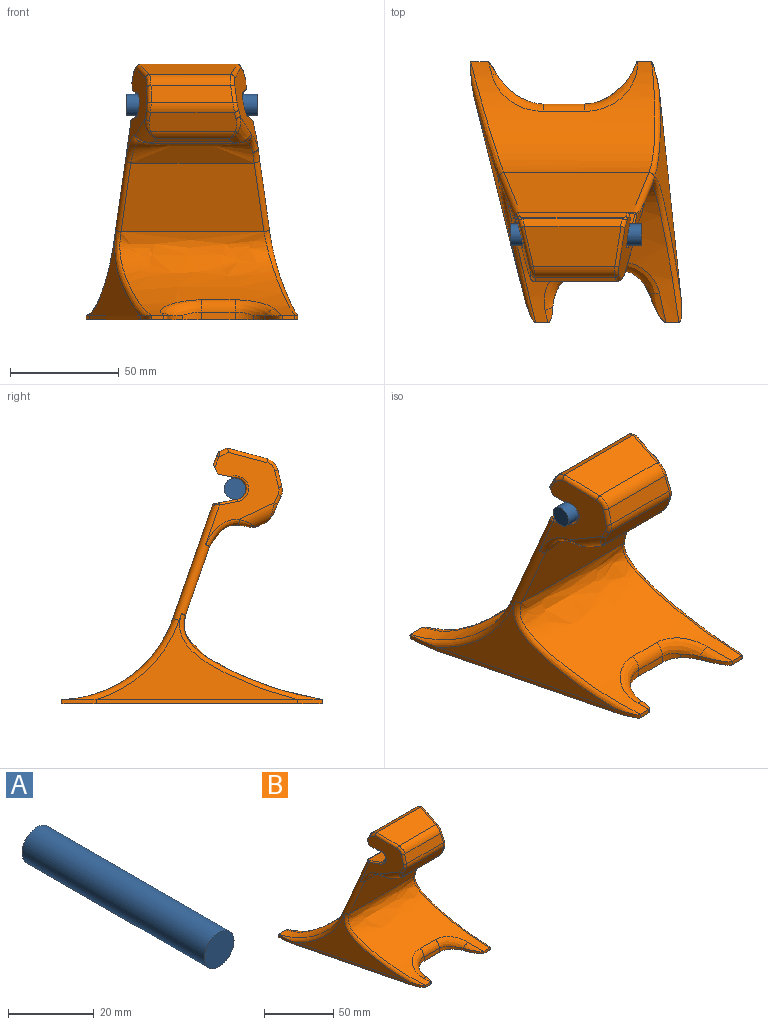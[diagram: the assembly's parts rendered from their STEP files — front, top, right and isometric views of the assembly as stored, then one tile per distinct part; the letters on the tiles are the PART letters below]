
ASSEMBLY  parts=2 mates=1
PART A: 3 faces, bbox 9.8x60x9.8 mm
  f0: cylinder r=4.9mm len=60mm, axis (0,1,0), area 1847.3mm2, adj f1,f2
  f1: plane 9.8x9.8mm, normal (0,-1,0), area 75.4mm2, adj f0
  f2: plane 9.8x9.8mm, normal (0,1,0), area 75.4mm2, adj f0
PART B: 107 faces, bbox 101.3x139.5x139.7 mm
  f0: bspline ~123.3x69.06mm, area 557mm2, adj f30,f62,f63,f69,f70,f71,f72,f77
  f1: plane 42.46x33.79mm, normal (-0.97,-0.24,0.05), area 579.7mm2, adj f13,f19,f31,f33,f65,f67,f73,f74
  f2: plane 95.15x39.86mm, normal (0.98,0.1,0.17), area 1113.8mm2, adj f26,f27,f28,f58
  f3: plane 92.77x39.56mm, normal (-0.97,-0.24,0.05), area 1096.3mm2, adj f32,f33,f34,f50
  f4: cylinder r=55.44mm len=83.31mm, axis (-1,0,0), area 3679.6mm2, adj f10,f26,f34,f40,f41,f42,f43,f52
  f5: plane 44.65x18.45mm, normal (0,-0.26,0.97), area 781.6mm2, adj f18,f69,f70,f75,f76,f78
  f6: plane 40.4x8.66mm, normal (0,-0.91,-0.41), area 376.6mm2, adj f72,f73,f81,f83,f88,f91
  f7: extruded ~56.76x17.9mm, area 1162.2mm2, adj f8,f29,f30,f31,f84,f89,f92
  f8: plane 65.74x31.62mm, normal (0,-0.94,-0.33), area 2052.5mm2, adj f7,f9,f27,f29,f31,f33
  f9: extruded ~80.56x63.79mm, area 4079.8mm2, adj f8,f27,f28,f32,f33,f35,f36,f37
  f10: plane 66.6x52.31mm, normal (0,0.94,0.33), area 3282.4mm2, adj f4,f27,f33,f66
  f11: plane 54.15x10.49mm, normal (0,0.18,0.98), area 555.2mm2, adj f12,f63,f64,f66,f67,f68
  f12: cylinder r=5mm len=49.57mm, axis (-1,0,0), area 661.6mm2, adj f11,f13,f62,f65
  f13: plane 51.77x9.13mm, normal (0,0.21,-0.98), area 445.6mm2, adj f1,f12,f19,f65,f95,f96
  f14: plane 50.31x5.37mm, normal (0,0.91,0.41), area 287.8mm2, adj f19,f96,f97,f98,f99,f100,f101
  f15: plane 10.19x3.56mm, normal (0.98,0.1,0.17), area 6.8mm2, adj f27,f29,f104
  f16: plane 37.7x7.8mm, normal (0,-0.97,0.23), area 298mm2, adj f71,f74,f78,f81
  f17: plane 35.23x3.01mm, normal (0,-0.43,-0.9), area 114.7mm2, adj f85,f88,f89,f94
  f18: plane 45.95x3.46mm, normal (0,0.43,0.9), area 172.7mm2, adj f5,f69,f76,f99
  f19: plane 51.94x4.81mm, normal (0,0.89,-0.45), area 258.7mm2, adj f1,f13,f14,f96,f101
  f20: plane 19.04x2.1mm, normal (0,1,0), area 40mm2, adj f22,f23,f41,f61
  f21: plane 15.54x3.61mm, normal (0,-1,0), area 56.1mm2, adj f24,f25,f38,f61
  f22: cylinder r=18.29mm len=2.41mm, axis (0,0,1), area 4.9mm2, adj f20,f40,f55,f61
  f23: cylinder r=18.29mm len=2.41mm, axis (0,0,1), area 4.9mm2, adj f20,f43,f54,f61
  f24: cylinder r=13.01mm len=8.48mm, axis (0,0,1), area 25.9mm2, adj f21,f36,f45,f61
  f25: cylinder r=13.01mm len=8.48mm, axis (0,0,1), area 25.9mm2, adj f21,f39,f46,f61
  f26: bspline ~53.44x39.28mm, area 212.6mm2, adj f2,f4,f27,f57
  f27: cylinder r=2.5mm len=54.06mm, axis (0.13,0.33,-0.94), area 334.9mm2, adj f2,f8,f9,f10,f15,f26,f28,f29
  f28: bspline ~68.14x42.43mm, area 295.3mm2, adj f2,f9,f27,f59
  f29: bspline ~8.97x7.02mm, area 26.7mm2, adj f7,f8,f15,f27,f102,f103
  f30: bspline ~12.73x8.67mm, area 48.5mm2, adj f0,f7,f92,f102
  f31: bspline ~17.65x13.1mm, area 71.1mm2, adj f1,f7,f8,f33,f84
  f32: bspline ~67.71x42.29mm, area 277.8mm2, adj f3,f9,f33,f49
  f33: cylinder r=2.5mm len=54.81mm, axis (-0.13,0.33,-0.94), area 365.3mm2, adj f1,f3,f8,f9,f10,f31,f32,f34
  f34: bspline ~54.1x39.59mm, area 261.5mm2, adj f3,f4,f33,f51
  f35: bspline ~19.35x9.82mm, area 40.6mm2, adj f9,f36,f44
  f36: bspline ~21.47x16.35mm, area 157mm2, adj f9,f24,f35,f38,f45
  f37: bspline ~16.44x9.13mm, area 11.6mm2, adj f9,f39,f47
  f38: cylinder r=6mm len=15.54mm, axis (-1,0,0), area 113.4mm2, adj f9,f21,f36,f39
  f39: bspline ~23.47x21.67mm, area 192.3mm2, adj f9,f25,f37,f38,f46
  f40: bspline ~26.88x24.14mm, area 140.9mm2, adj f4,f22,f41,f55
  f41: cylinder r=6mm len=19.04mm, axis (-1,0,0), area 128mm2, adj f4,f20,f40,f43
  f42: bspline ~21.17x10.9mm, area 6.9mm2, adj f4,f43,f53
  f43: bspline ~26.6x19.5mm, area 142.6mm2, adj f4,f23,f41,f42,f54
  f44: extruded ~13.18x7.87mm, area 31.4mm2, adj f35,f45,f60,f61
  f45: extruded ~7.66x5.23mm, area 18.8mm2, adj f24,f36,f44,f61
  f46: extruded ~14.04x6.51mm, area 31.8mm2, adj f25,f39,f47,f61
  f47: extruded ~6.8x2.31mm, area 15.2mm2, adj f37,f46,f48,f61
  f48: plane 5.63x2mm, normal (0,-1,0), area 11.3mm2, adj f9,f47,f49,f61
  f49: extruded ~11.4x5.19mm, area 25.6mm2, adj f32,f48,f50,f61
  f50: plane 92.76x23.19mm, normal (-0.97,-0.24,0), area 191.2mm2, adj f3,f49,f51,f61
  f51: extruded ~15.85x2mm, area 32mm2, adj f34,f50,f52,f61
  f52: plane 8.2x2mm, normal (0,1,0), area 16.4mm2, adj f4,f51,f53,f61
  f53: extruded ~5.64x3.73mm, area 13.6mm2, adj f42,f52,f54,f61
  f54: extruded ~19.1x13.71mm, area 48.5mm2, adj f23,f43,f53,f61
  f55: extruded ~21.86x19.35mm, area 61.2mm2, adj f22,f40,f56,f61
  f56: plane 6.58x2mm, normal (0,1,0), area 13.2mm2, adj f4,f55,f57,f61
  f57: extruded ~13.92x3.57mm, area 28.9mm2, adj f26,f56,f58,f61
  f58: plane 95.14x10mm, normal (0.99,0.1,0), area 191.3mm2, adj f2,f57,f59,f61
  f59: extruded ~10.94x2mm, area 22.7mm2, adj f28,f58,f60,f61
  f60: plane 5.94x2mm, normal (0,-1,0), area 11.9mm2, adj f9,f44,f59,f61
  f61: plane 120.34x97.64mm, normal (0,0,-1), area 7411.2mm2, adj f20,f21,f22,f23,f24,f25,f44,f45
  f62: bspline ~12x6.11mm, area 25.5mm2, adj f0,f12,f63,f95
  f63: bspline ~45x11.22mm, area 15.2mm2, adj f0,f11,f62,f106
  f64: bspline ~1.45x1.09mm, area 1.4mm2, adj f11,f27,f66,f106
  f65: bspline ~11.9x8.36mm, area 28.8mm2, adj f1,f12,f13,f67
  f66: cylinder r=1mm len=51.88mm, axis (-1,0,0), area 54.6mm2, adj f10,f11,f64,f68
  f67: cylinder r=1mm len=8.86mm, axis (0.25,-0.95,0.18), area 13.8mm2, adj f1,f11,f65,f68
  f68: bspline ~3.24x2.39mm, area 4.6mm2, adj f11,f33,f66,f67
  f69: bspline ~54.51x27.21mm, area 12.6mm2, adj f0,f5,f18,f70,f98
  f70: bspline ~44.83x13.31mm, area 51mm2, adj f0,f5,f69,f77
  f71: bspline ~22.73x6.95mm, area 21.7mm2, adj f0,f16,f77,f82
  f72: bspline ~26.95x13.11mm, area 9.2mm2, adj f0,f6,f82,f91
  f73: cylinder r=2mm len=4.65mm, axis (-0.15,0.4,-0.9), area 11.3mm2, adj f1,f6,f80,f83
  f74: cylinder r=2mm len=8.16mm, axis (0.01,-0.23,-0.97), area 21.2mm2, adj f1,f16,f79,f80
  f75: cylinder r=2mm len=18.57mm, axis (0.22,-0.94,-0.25), area 55.9mm2, adj f1,f5,f76,f79
  f76: cylinder r=2mm len=6.15mm, axis (-0.24,0.88,-0.42), area 13.8mm2, adj f1,f5,f18,f75,f100
  f77: bspline ~6.03x5.48mm, area 17.5mm2, adj f0,f70,f71,f78
  f78: cylinder r=7mm len=37.39mm, axis (1,0,0), area 278.8mm2, adj f5,f16,f77,f79
  f79: bspline ~5.88x5.79mm, area 18.4mm2, adj f1,f74,f75,f78
  f80: bspline ~4.49x2.18mm, area 10.9mm2, adj f1,f73,f74,f81
  f81: cylinder r=7mm len=38.55mm, axis (1,0,0), area 174.8mm2, adj f6,f16,f80,f82
  f82: bspline ~5.36x2.7mm, area 11.5mm2, adj f0,f71,f72,f81
  f83: bspline ~6.27x3.09mm, area 13.5mm2, adj f6,f73,f85,f86
  f84: bspline ~8.37x6.43mm, area 22.5mm2, adj f7,f31,f85,f87
  f85: cylinder r=7mm len=17.89mm, axis (0.24,-0.88,0.42), area 112.2mm2, adj f1,f17,f83,f84,f86,f87
  f86: bspline ~4.27x4.19mm, area 3.1mm2, adj f83,f85,f88
  f87: bspline ~5.98x5.57mm, area 5.4mm2, adj f84,f85,f89
  f88: cylinder r=7mm len=38.62mm, axis (1,0,0), area 179.1mm2, adj f6,f17,f86,f90
  f89: cylinder r=7mm len=42.71mm, axis (-1,0,0), area 192.4mm2, adj f7,f17,f87,f93
  f90: bspline ~4.85x4.62mm, area 3.1mm2, adj f88,f91,f94
  f91: bspline ~9.82x4.59mm, area 16.8mm2, adj f6,f72,f90,f94
  f92: bspline ~9.64x7.07mm, area 28.3mm2, adj f7,f30,f93,f94
  f93: bspline ~5.94x5.51mm, area 5.6mm2, adj f89,f92,f94
  f94: bspline ~74.71x41.45mm, area 132.1mm2, adj f0,f17,f90,f91,f92,f93
  f95: bspline ~28.47x7.21mm, area 15.8mm2, adj f0,f13,f62,f96
  f96: bspline ~42.01x22.15mm, area 8.7mm2, adj f0,f13,f14,f19,f95,f97
  f97: bspline ~41.79x19.51mm, area 7.2mm2, adj f0,f14,f96,f98
  f98: bspline ~2.89x2.83mm, area 3.1mm2, adj f14,f69,f97,f99
  f99: cylinder r=1mm len=45.95mm, axis (-1,0,0), area 32.4mm2, adj f14,f18,f98,f100
  f100: bspline ~2.34x2.32mm, area 3.6mm2, adj f14,f76,f99,f101
  f101: cylinder r=1mm len=5.27mm, axis (0.15,-0.4,0.9), area 8.6mm2, adj f1,f14,f19,f100
  f102: bspline ~2.49x2.17mm, area 0.3mm2, adj f29,f30,f103
  f103: bspline ~0.86x0.48mm, area 0.1mm2, adj f0,f29,f102,f104
  f104: bspline ~15.44x2.74mm, area 1.3mm2, adj f0,f15,f103,f105
  f105: bspline ~9.93x2.63mm, area 5.9mm2, adj f0,f27,f104,f106
  f106: sphere r=1mm, area 0.8mm2, adj f63,f64,f105
PLACE A rot(axis=(0.58,-0.58,0.58),120deg) t=(-19.82,76.18,87.34)mm
PLACE B at identity
MATE cylindrical A.f0 <-> B.f12  axis (-1,0,0) through (10.18,33.35,63.81)mm
